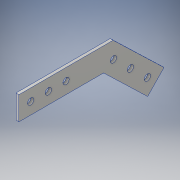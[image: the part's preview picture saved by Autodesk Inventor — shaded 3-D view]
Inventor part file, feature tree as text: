
AUTODESK INVENTOR PART (.ipt)
format: ipt  version: 2016 (Build 200138000, 138)  size: 128,000 bytes
history: native  units: in
note: dims shown in document units (in); Inventor stores cm internally (conversion verified against a paired STEP export)
features: extrude x2, sketch x2
ambient origin geometry x8: Origin, YZ Plane, XZ Plane, XY Plane, X Axis, Y Axis, Z Axis, Center Point
bodies: Solid1 (feature_tree)
feature tree (4):
  extrude  "Extrusion1"  Depth=1.0in
  extrude  "Extrusion2"  Depth=0.125in
  sketch  "Sketch1"  dims[d0=4.0in d1=1.0in]
  sketch  "Sketch2"  dims[d2=1.0in d3=3.0in d4=0.9351in d5=0.125in d6=0.0in d7=0.2656in d8=0.2656in d9=0.2656in d10=0.5in d11=0.75in d12=0.75in d13=0.125in d14=0.0in d15=0.2656in d16=0.2656in d17=0.2656in d18=0.5in d19=0.5in d20=0.5in d21=0.5in d22=1.5in d23=2.5in]
